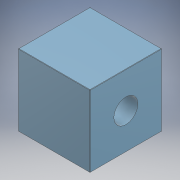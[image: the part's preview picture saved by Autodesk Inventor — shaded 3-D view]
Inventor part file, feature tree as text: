
AUTODESK INVENTOR PART (.ipt)
format: ipt  version: 2022 (Build 260153000, 153)  size: 145,408 bytes
history: native  units: mm
features: sketch x3, hole x2, extrude x1, fillet x1
ambient origin geometry x8: Origin, YZ Plane, XZ Plane, XY Plane, X Axis, Y Axis, Z Axis, Center Point
bodies: Solid1 (feature_tree)
feature tree (7):
  extrude  "Box"  Depth=198.0mm
  hole  "DecAxisHole"  [1 undecoded]
  hole  "BoltHoles"  [1 undecoded]
  fillet  "Fillet1"  [1 undecoded]
  sketch  "Sketch1"  dims[d0=198.0mm d1=198.0mm]
  sketch  "Sketch2"  dims[d2=198.0mm d3=0.0mm]
  sketch  "Sketch3"  dims[d4=66.0mm d5=16.0mm d6=4.0mm d7=2.0mm d8=90.0deg d9=8.0mm d10=0.0mm d11=8.0mm d12=6.0mm d13=4.0mm d14=2.0mm d15=90.0deg d16=24.0mm d17=20.594885mm d18=1.0mm]
note: 3 required parameter values undecoded (feature->parameter linkage not recoverable at this tier; creation-order binding heuristic only, values carry confidence <= 0.55)
